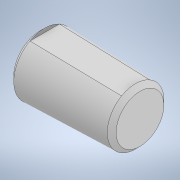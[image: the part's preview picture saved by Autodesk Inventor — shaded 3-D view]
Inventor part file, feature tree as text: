
AUTODESK INVENTOR PART (.ipt)
format: ipt  version: 2021.1 (Build 251245010, 245A)  size: 117,248 bytes
history: native  units: mm
features: other x1, extrude x1, sketch x1, imported_body x1
ambient origin geometry x8: Origin, YZ Plane, XZ Plane, XY Plane, X Axis, Y Axis, Z Axis, Center Point
bodies: Body1 (feature_tree)
feature tree (4):
  other  "Твердое тело1"
  extrude  "Выдавливание1"  Depth=10.0mm TaperAngle=0.0deg
  sketch  "Эскиз1"
  imported_body  "БазТело1"
